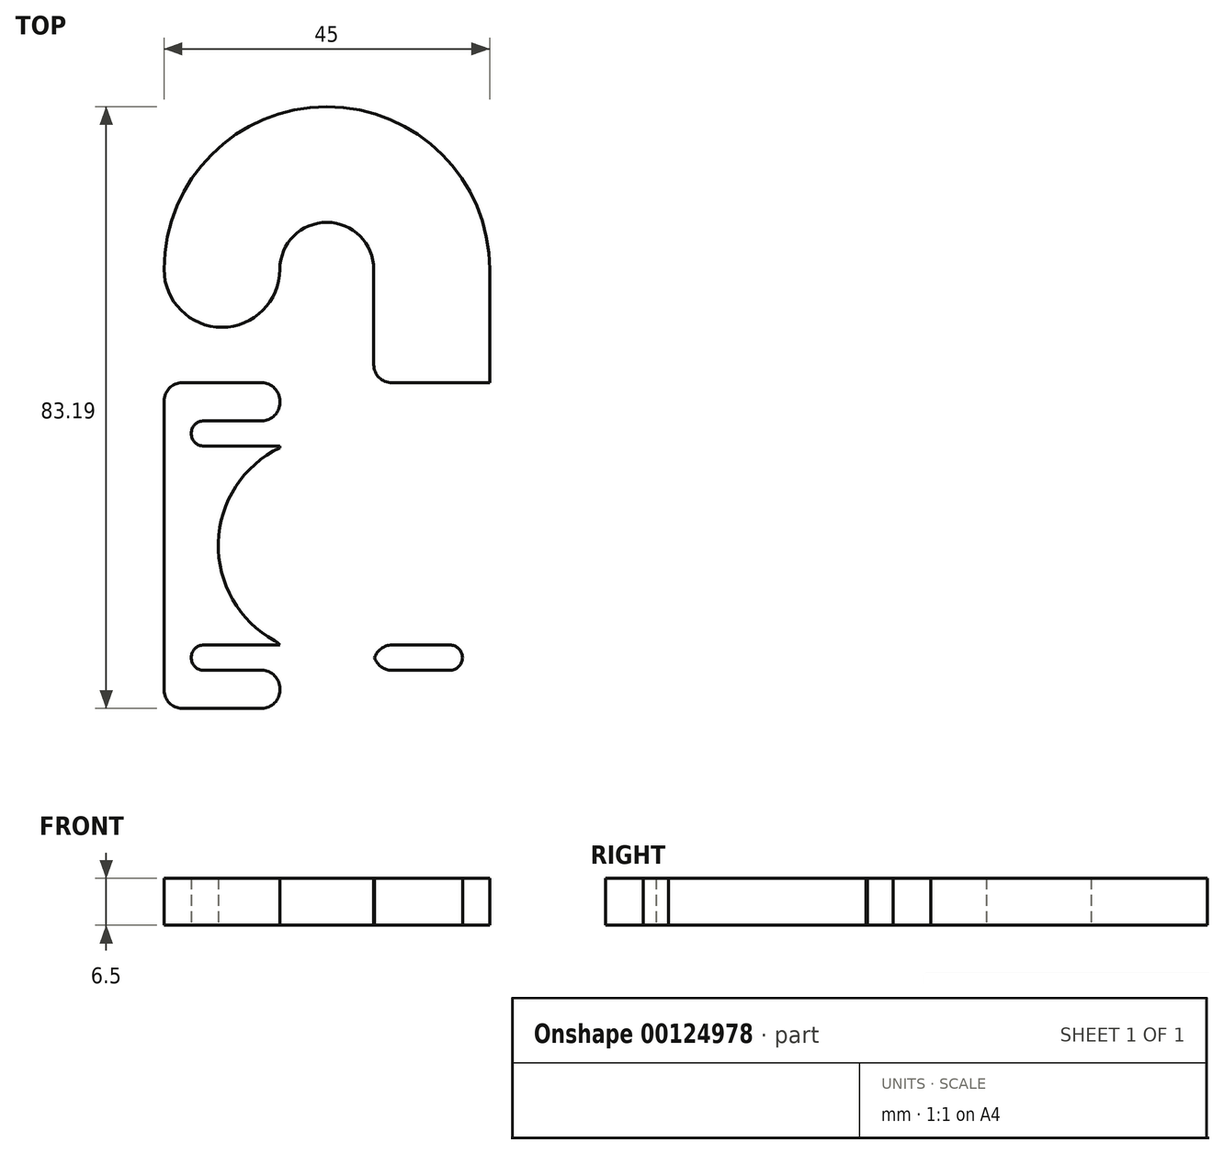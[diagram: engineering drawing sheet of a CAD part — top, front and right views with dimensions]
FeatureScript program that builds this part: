
annotation { "Feature Type Name" : "Feature", "Feature Type Description" : "" }
export const myFeature = defineFeature(function(context is Context, id is Id, definition is map)
    precondition{}
    {
        {
            var Q0;
            Q0=qCreatedBy(makeId("Top.planeOp"),FACE);
            var sketch = newSketch(context, id + "F0", { "sketchPlane" : qUnion([Q0])});
            skLineSegment(sketch, "E0.top", {"start": v(-22.5, -22.5) * mm, "end": v(22.5, -22.5) * mm});
            skLineSegment(sketch, "E0.left", {"start": v(-22.5, 22.5) * mm, "end": v(-22.5, -22.5) * mm});
            skLineSegment(sketch, "E1", {"start": v(-17, -15.5) * mm, "end": v(-5, -15.5) * mm, "construction": true});
            skArc(sketch, "E2.0.startCap", {"start": v(-17, -17.25) * mm, "mid": v(-18.75, -15.5) * mm, "end": v(-17, -13.75) * mm});
            skArc(sketch, "E2.0.endCap", {"start": v(-5, -13.75) * mm, "mid": v(-3.25, -15.5) * mm, "end": v(-5, -17.25) * mm});
            skLineSegment(sketch, "E2.0.left", {"start": v(-17, -13.75) * mm, "end": v(-5, -13.75) * mm});
            skLineSegment(sketch, "E2.0.right", {"start": v(-17, -17.25) * mm, "end": v(-5, -17.25) * mm});
            skArc(sketch, "E3.1.0.0", {"start": v(5, -17.25) * mm, "mid": v(3.25, -15.5) * mm, "end": v(5, -13.75) * mm});
            skLineSegment(sketch, "E3.1.0.1", {"start": v(5, -17.25) * mm, "end": v(17, -17.25) * mm});
            skArc(sketch, "E3.1.0.2", {"start": v(17, -13.75) * mm, "mid": v(18.75, -15.5) * mm, "end": v(17, -17.25) * mm});
            skLineSegment(sketch, "E3.1.0.3", {"start": v(5, -13.75) * mm, "end": v(17, -13.75) * mm});
            skLineSegment(sketch, "E3.direction1", {"start": v(-17, -17.25) * mm, "end": v(5, -17.25) * mm, "construction": true});
            skCircle(sketch, "E4", {"center": v(0, 0) * mm, "radius": 15 * mm});
            skLineSegment(sketch, "E5", {"start": v(-22.5, 22.5) * mm, "end": v(22.5, 22.5) * mm});
            skLineSegment(sketch, "E6", {"start": v(22.5, 22.5) * mm, "end": v(22.5, -22.5) * mm});
            skArc(sketch, "E7.0.1.0", {"start": v(-17, 13.75) * mm, "mid": v(-18.75, 15.5) * mm, "end": v(-17, 17.25) * mm});
            skLineSegment(sketch, "E7.0.1.1", {"start": v(-17, 17.25) * mm, "end": v(-5, 17.25) * mm});
            skArc(sketch, "E7.0.1.2", {"start": v(-5, 17.25) * mm, "mid": v(-3.25, 15.5) * mm, "end": v(-5, 13.75) * mm});
            skLineSegment(sketch, "E7.0.1.3", {"start": v(-17, 13.75) * mm, "end": v(-5, 13.75) * mm});
            skLineSegment(sketch, "E7.direction1", {"start": v(-17, -17.25) * mm, "end": v(4.2, -17.25) * mm, "construction": true});
            skLineSegment(sketch, "E7.direction2", {"start": v(-17, -17.25) * mm, "end": v(-17, 13.75) * mm, "construction": true});
            skArc(sketch, "E8.1.0.0", {"start": v(17, 17.25) * mm, "mid": v(18.75, 15.5) * mm, "end": v(17, 13.75) * mm});
            skLineSegment(sketch, "E8.1.0.1", {"start": v(5, 13.75) * mm, "end": v(17, 13.75) * mm});
            skArc(sketch, "E8.1.0.2", {"start": v(5, 13.75) * mm, "mid": v(3.25, 15.5) * mm, "end": v(5, 17.25) * mm});
            skLineSegment(sketch, "E8.1.0.3", {"start": v(5, 17.25) * mm, "end": v(17, 17.25) * mm});
            skLineSegment(sketch, "E8.direction1", {"start": v(-5, 13.75) * mm, "end": v(17, 13.75) * mm, "construction": true});
            skLineSegment(sketch, "E9", {"start": v(22.5, 0) * mm, "end": v(-22.5, 0) * mm, "construction": true});
            skLineSegment(sketch, "E10", {"start": v(-5, 15.5) * mm, "end": v(5, -15.5) * mm, "construction": true});
            skLineSegment(sketch, "E11", {"start": v(5, 15.5) * mm, "end": v(-5, -15.5) * mm, "construction": true});
            skPoint(sketch, "E12.endSnap0", {"position": v(-6, -17.25) * mm});
            skLineSegment(sketch, "E13", {"start": v(0, 22.5) * mm, "end": v(0, -22.5) * mm, "construction": true});
            skLineSegment(sketch, "E14", {"start": v(6.5, 22.5) * mm, "end": v(6.5, 13.52) * mm});
            skLineSegment(sketch, "E15", {"start": v(6.5, -13.52) * mm, "end": v(6.5, -22.5) * mm});
            skLineSegment(sketch, "E16.MirrorCS", {"start": v(-6.5, -13.52) * mm, "end": v(-6.5, -22.5) * mm});
            skLineSegment(sketch, "E17.MirrorCS", {"start": v(-6.5, 22.5) * mm, "end": v(-6.5, 13.52) * mm});
            skLineSegment(sketch, "E18", {"start": v(22.5, 22.5) * mm, "end": v(22.5, 38.19) * mm});
            skArc(sketch, "E19", {"start": v(22.5, 38.19) * mm, "mid": v(0, 60.69) * mm, "end": v(-22.5, 38.19) * mm});
            skArc(sketch, "E20.0", {"start": v(6.5, 38.19) * mm, "mid": v(0, 44.68) * mm, "end": v(-6.5, 38.19) * mm});
            skLineSegment(sketch, "E20.1", {"start": v(6.5, 22.5) * mm, "end": v(6.5, 38.19) * mm});
            skArc(sketch, "E21", {"start": v(-6.5, 38.19) * mm, "mid": v(-14.5, 30.18) * mm, "end": v(-22.5, 38.19) * mm});
            skSolve(sketch);
        }
        {
            var Q0;
            {var subQ4=sQuery(id+"F0.wireOp",EDGE,"E0.left");Q0=makeQuery(id+"F0.imprint","IMPRINT",FACE,{"disambiguationData":[TD([[makeQuery(id+"F0.imprint","IMPRINT",EDGE,{"derivedFrom":subQ4}),1.0]])]});}
            var Q1;
            {var subQ5=sQuery(id+"F0.wireOp",EDGE,"E3.1.0.2");Q1=makeQuery(id+"F0.imprint","IMPRINT",FACE,{"disambiguationData":[TD([[makeQuery(id+"F0.imprint","IMPRINT",EDGE,{"derivedFrom":subQ5}),1.0]])]});}
            var Q2;
            {var subQ0=sQuery(id+"F0.wireOp",EDGE,"E18");Q2=makeQuery(id+"F0.imprint","IMPRINT",FACE,{"disambiguationData":[TD([[makeQuery(id+"F0.imprint","IMPRINT",EDGE,{"derivedFrom":subQ0}),1.0]])]});}
            extrude(context, id + "F1", {"entities" : qUnion([Q0, Q1, Q2]), "depth" : 6.5 * mm, "offsetDistance" : 25 * mm});
        }
        {
            var Q0;
            Q0=qCreatedBy(makeId("Right.planeOp"),FACE);
            var sketch = newSketch(context, id + "F2", { "sketchPlane" : qUnion([Q0])});
            skLineSegment(sketch, "E22.bottom", {"start": v(-11.01, 12.56) * mm, "end": v(11.01, 12.56) * mm});
            skLineSegment(sketch, "E22.top", {"start": v(-11.01, 3.62) * mm, "end": v(11.01, 3.62) * mm});
            skLineSegment(sketch, "E22.left", {"start": v(-11.01, 12.56) * mm, "end": v(-11.01, 3.62) * mm});
            skLineSegment(sketch, "E22.right", {"start": v(11.01, 12.56) * mm, "end": v(11.01, 3.62) * mm});
            skLineSegment(sketch, "E23", {"start": v(0, 0) * mm, "end": v(0, 3.62) * mm, "construction": true});
            skSolve(sketch);
        }
        {
            var Q0;
            Q0 = qSketchRegion(id + "F2", true);
            extrude(context, id + "F3", {"entities" : qUnion([Q0]), "operationType" : NewBodyOperationType.REMOVE, "depth" : 33.6 * mm, "offsetDistance" : 25 * mm});
        }
        {
            var Q0;
            Q0=makeQuery(id+"F1.opExtrude","SWEPT_EDGE",EDGE,{"disambiguationData":[OSD([sQuery(id+"F0.wireOp",EDGE,"E0.top"),sQuery(id+"F0.wireOp",EDGE,"E6")])]});
            var Q1;
            Q1=makeQuery(id+"F1.opExtrude","SWEPT_EDGE",EDGE,{"disambiguationData":[OSD([sQuery(id+"F0.wireOp",EDGE,"E0.top"),sQuery(id+"F0.wireOp",EDGE,"E16.MirrorCS")])]});
            var Q2;
            Q2=makeQuery(id+"F1.opExtrude","SWEPT_EDGE",EDGE,{"disambiguationData":[OSD([sQuery(id+"F0.wireOp",EDGE,"E0.top"),sQuery(id+"F0.wireOp",EDGE,"E0.left")])]});
            var Q3;
            Q3=makeQuery(id+"F1.opExtrude","SWEPT_EDGE",EDGE,{"disambiguationData":[OSD([sQuery(id+"F0.wireOp",EDGE,"E0.top"),sQuery(id+"F0.wireOp",EDGE,"E15")])]});
            var Q4;
            Q4=makeQuery(id+"F1.opExtrude","SWEPT_EDGE",EDGE,{"disambiguationData":[OSD([sQuery(id+"F0.wireOp",EDGE,"E7.0.1.0"),sQuery(id+"F0.wireOp",EDGE,"E7.0.1.1")])]});
            var Q5;
            Q5=makeQuery(id+"F1.opExtrude","SWEPT_EDGE",EDGE,{"disambiguationData":[OSD([sQuery(id+"F0.wireOp",EDGE,"E4"),sQuery(id+"F0.wireOp",EDGE,"E16.MirrorCS")])]});
            var Q6;
            Q6=makeQuery(id+"F1.opExtrude","SWEPT_EDGE",EDGE,{"disambiguationData":[OSD([sQuery(id+"F0.wireOp",EDGE,"E7.0.1.1"),sQuery(id+"F0.wireOp",EDGE,"E17.MirrorCS")])]});
            var Q7;
            Q7=makeQuery(id+"F1.opExtrude","SWEPT_EDGE",EDGE,{"disambiguationData":[OSD([sQuery(id+"F0.wireOp",EDGE,"E8.1.0.0"),sQuery(id+"F0.wireOp",EDGE,"E8.1.0.3")])]});
            var Q8;
            Q8=makeQuery(id+"F1.opExtrude","SWEPT_EDGE",EDGE,{"disambiguationData":[OSD([sQuery(id+"F0.wireOp",EDGE,"E7.0.1.0"),sQuery(id+"F0.wireOp",EDGE,"E7.0.1.3")])]});
            var Q9;
            Q9=makeQuery(id+"F1.opExtrude","SWEPT_EDGE",EDGE,{"disambiguationData":[OSD([sQuery(id+"F0.wireOp",EDGE,"E8.1.0.0"),sQuery(id+"F0.wireOp",EDGE,"E8.1.0.1")])]});
            var Q10;
            Q10=makeQuery(id+"F1.opExtrude","SWEPT_EDGE",EDGE,{"disambiguationData":[OSD([sQuery(id+"F0.wireOp",EDGE,"E3.1.0.2"),sQuery(id+"F0.wireOp",EDGE,"E3.1.0.3")])]});
            var Q11;
            Q11=makeQuery(id+"F1.opExtrude","SWEPT_EDGE",EDGE,{"disambiguationData":[OSD([sQuery(id+"F0.wireOp",EDGE,"E3.1.0.3"),sQuery(id+"F0.wireOp",EDGE,"E15")])]});
            var Q12;
            Q12=makeQuery(id+"F1.opExtrude","SWEPT_EDGE",EDGE,{"disambiguationData":[OSD([sQuery(id+"F0.wireOp",EDGE,"E2.0.startCap"),sQuery(id+"F0.wireOp",EDGE,"E2.0.left")])]});
            var Q13;
            Q13=makeQuery(id+"F1.opExtrude","SWEPT_EDGE",EDGE,{"disambiguationData":[OSD([sQuery(id+"F0.wireOp",EDGE,"E3.1.0.1"),sQuery(id+"F0.wireOp",EDGE,"E3.1.0.2")])]});
            var Q14;
            Q14=makeQuery(id+"F1.opExtrude","SWEPT_EDGE",EDGE,{"disambiguationData":[OSD([sQuery(id+"F0.wireOp",EDGE,"E3.1.0.1"),sQuery(id+"F0.wireOp",EDGE,"E15")])]});
            var Q15;
            Q15=makeQuery(id+"F1.opExtrude","SWEPT_EDGE",EDGE,{"disambiguationData":[OSD([sQuery(id+"F0.wireOp",EDGE,"E2.0.startCap"),sQuery(id+"F0.wireOp",EDGE,"E2.0.right")])]});
            var Q16;
            Q16=makeQuery(id+"F1.opExtrude","SWEPT_EDGE",EDGE,{"disambiguationData":[OSD([sQuery(id+"F0.wireOp",EDGE,"E2.0.right"),sQuery(id+"F0.wireOp",EDGE,"E16.MirrorCS")])]});
            var Q17;
            Q17=makeQuery(id+"F1.opExtrude","SWEPT_EDGE",EDGE,{"disambiguationData":[OSD([sQuery(id+"F0.wireOp",EDGE,"E0.left"),sQuery(id+"F0.wireOp",EDGE,"E5")])]});
            var Q18;
            Q18=makeQuery(id+"F1.opExtrude","SWEPT_EDGE",EDGE,{"disambiguationData":[OSD([sQuery(id+"F0.wireOp",EDGE,"E5"),sQuery(id+"F0.wireOp",EDGE,"E17.MirrorCS")])]});
            var Q19;
            Q19=makeQuery(id+"F1.opExtrude","SWEPT_EDGE",EDGE,{"disambiguationData":[OSD([sQuery(id+"F0.wireOp",EDGE,"E8.1.0.3"),sQuery(id+"F0.wireOp",EDGE,"E14")])]});
            var Q20;
            Q20=makeQuery(id+"F3.boolean.opBoolean","COPY",EDGE,{"derivedFrom":makeQuery(id+"F3.opExtrude","SWEPT_EDGE",EDGE,{"disambiguationData":[OSD([sQuery(id+"F2.wireOp",EDGE,"E22.top"),sQuery(id+"F2.wireOp",EDGE,"E22.right")])]})});
            var Q21;
            Q21=makeQuery(id+"F3.boolean.opBoolean","COPY",EDGE,{"derivedFrom":makeQuery(id+"F3.opExtrude","SWEPT_EDGE",EDGE,{"disambiguationData":[OSD([sQuery(id+"F2.wireOp",EDGE,"E22.top"),sQuery(id+"F2.wireOp",EDGE,"E22.left")])]})});
            fillet(context, id + "F4", {"entities" : qUnion([Q0, Q1, Q2, Q3, Q4, Q5, Q6, Q7, Q8, Q9, Q10, Q11, Q12, Q13, Q14, Q15, Q16, Q17, Q18, Q19, Q20, Q21]), "radius" : 2.5 * mm, "tangentPropagation" : true, "allowEdgeOverflow" : false});
        }
    });
